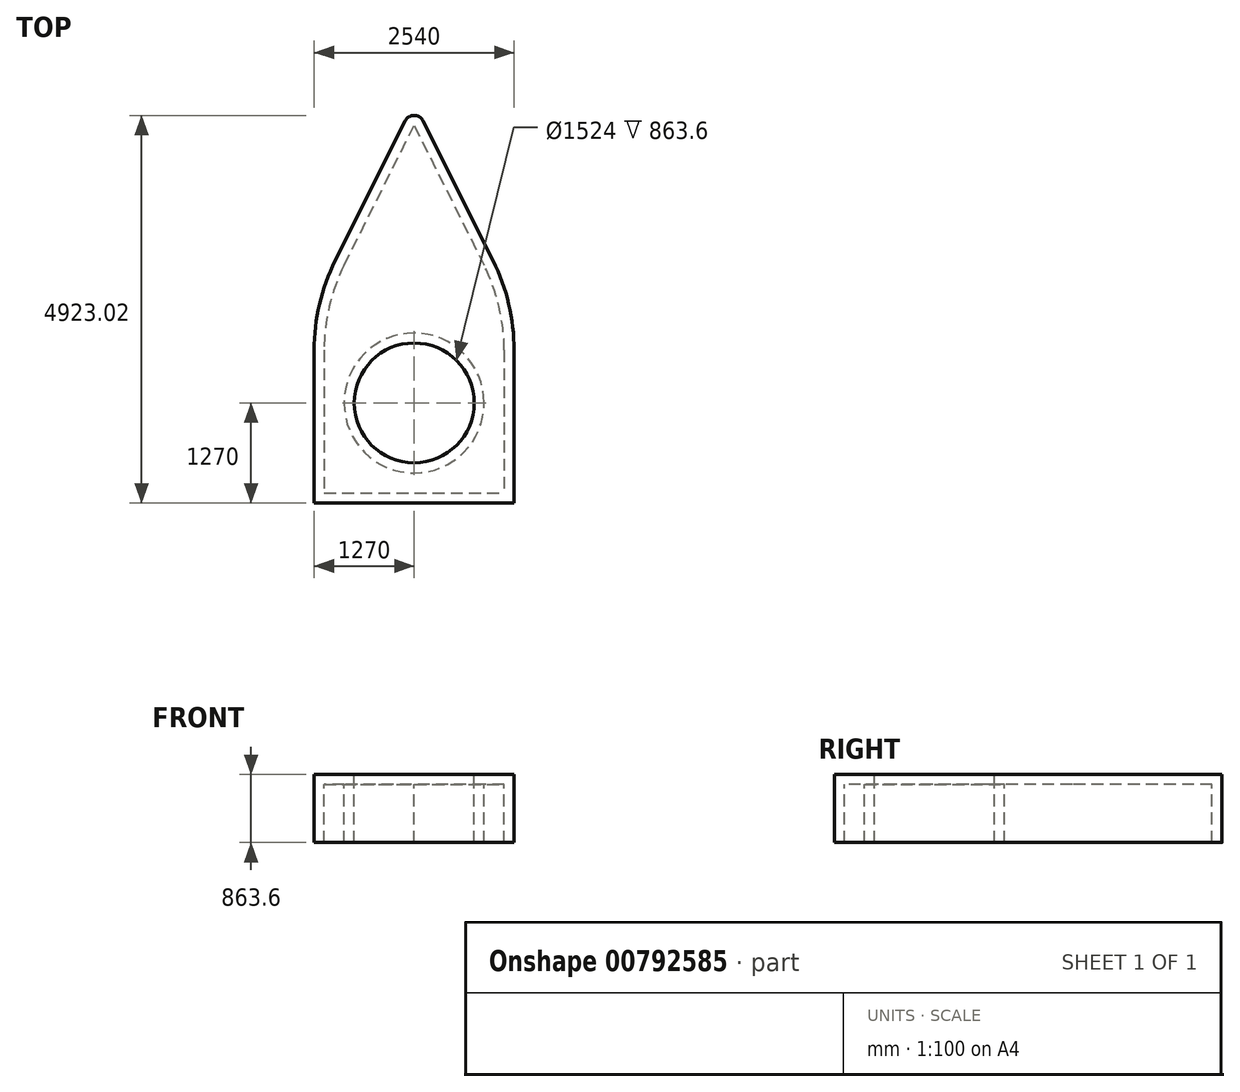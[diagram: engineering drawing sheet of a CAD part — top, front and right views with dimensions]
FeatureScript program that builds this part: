
annotation { "Feature Type Name" : "Feature", "Feature Type Description" : "" }
export const myFeature = defineFeature(function(context is Context, id is Id, definition is map)
    precondition{}
    {
        {
            var Q0;
            Q0=qCreatedBy(makeId("Top.planeOp"),FACE);
            var sketch = newSketch(context, id + "F0", { "sketchPlane" : qUnion([Q0])});
            skLineSegment(sketch, "E0.bottom", {"start": v(-1270, 1270) * mm, "end": v(1270, 1270) * mm});
            skLineSegment(sketch, "E0.top", {"start": v(-1270, -1270) * mm, "end": v(1270, -1270) * mm});
            skLineSegment(sketch, "E0.left", {"start": v(-1270, 1270) * mm, "end": v(-1270, -1270) * mm});
            skLineSegment(sketch, "E0.right", {"start": v(1270, 1270) * mm, "end": v(1270, -1270) * mm});
            skCircle(sketch, "E1", {"center": v(0, 0) * mm, "radius": 762 * mm});
            skLineSegment(sketch, "E2", {"start": v(-1270, 1270) * mm, "end": v(0, 3810) * mm});
            skLineSegment(sketch, "E3", {"start": v(0, 3810) * mm, "end": v(1270, 1270) * mm});
            skLineSegment(sketch, "E4", {"start": v(-1270, 1270) * mm, "end": v(1270, -1270) * mm, "construction": true});
            skSolve(sketch);
        }
        {
            var Q0;
            Q0=makeQuery(id+"F0.imprint","IMPRINT",FACE,{"disambiguationData":[TD([[makeQuery(id+"F0.imprint","IMPRINT",EDGE,{"derivedFrom":sQuery(id+"F0.wireOp",EDGE,"E0.bottom")}),-1.0]])]});
            var Q1;
            Q1=makeQuery(id+"F0.imprint","IMPRINT",FACE,{"disambiguationData":[TD([[makeQuery(id+"F0.imprint","IMPRINT",EDGE,{"derivedFrom":sQuery(id+"F0.wireOp",EDGE,"E0.bottom")}),1.0]])]});
            extrude(context, id + "F1", {"entities" : qUnion([Q0, Q1]), "oppositeDirection" : true, "depth" : 863.6 * mm, "offsetDistance" : 25.4 * mm});
        }
        {
            var Q0;
            Q0=makeQuery(id+"F1.opExtrude","SWEPT_EDGE",EDGE,{"disambiguationData":[OSD([sQuery(id+"F0.wireOp",EDGE,"E0.bottom"),sQuery(id+"F0.wireOp",EDGE,"E0.left"),sQuery(id+"F0.wireOp",EDGE,"E2")])]});
            var Q1;
            Q1=makeQuery(id+"F1.opExtrude","SWEPT_EDGE",EDGE,{"disambiguationData":[OSD([sQuery(id+"F0.wireOp",EDGE,"E0.bottom"),sQuery(id+"F0.wireOp",EDGE,"E0.right"),sQuery(id+"F0.wireOp",EDGE,"E3")])]});
            fillet(context, id + "F2", {"entities" : qUnion([Q0, Q1]), "radius" : 2540 * mm, "tangentPropagation" : true, "allowEdgeOverflow" : false});
        }
        {
            var Q0;
            Q0=makeQuery(id+"F1.opExtrude","CAP_FACE",FACE,{"disambiguationData":[OSD([sQuery(id+"F0.wireOp",EDGE,"E0.top"),sQuery(id+"F0.wireOp",EDGE,"E0.left"),sQuery(id+"F0.wireOp",EDGE,"E0.right"),sQuery(id+"F0.wireOp",EDGE,"E1"),sQuery(id+"F0.wireOp",EDGE,"E2"),sQuery(id+"F0.wireOp",EDGE,"E3")])],"isStart":false});
            shell(context, id + "F3", {"entities" : qUnion([Q0]), "thickness" : 127 * mm});
        }
        {
            var Q0;
            Q0=makeQuery(id+"F1.opExtrude","SWEPT_EDGE",EDGE,{"disambiguationData":[OSD([sQuery(id+"F0.wireOp",EDGE,"E2"),sQuery(id+"F0.wireOp",EDGE,"E3")])]});
            fillet(context, id + "F4", {"entities" : qUnion([Q0]), "radius" : 127 * mm, "tangentPropagation" : true, "allowEdgeOverflow" : false});
        }
    });
